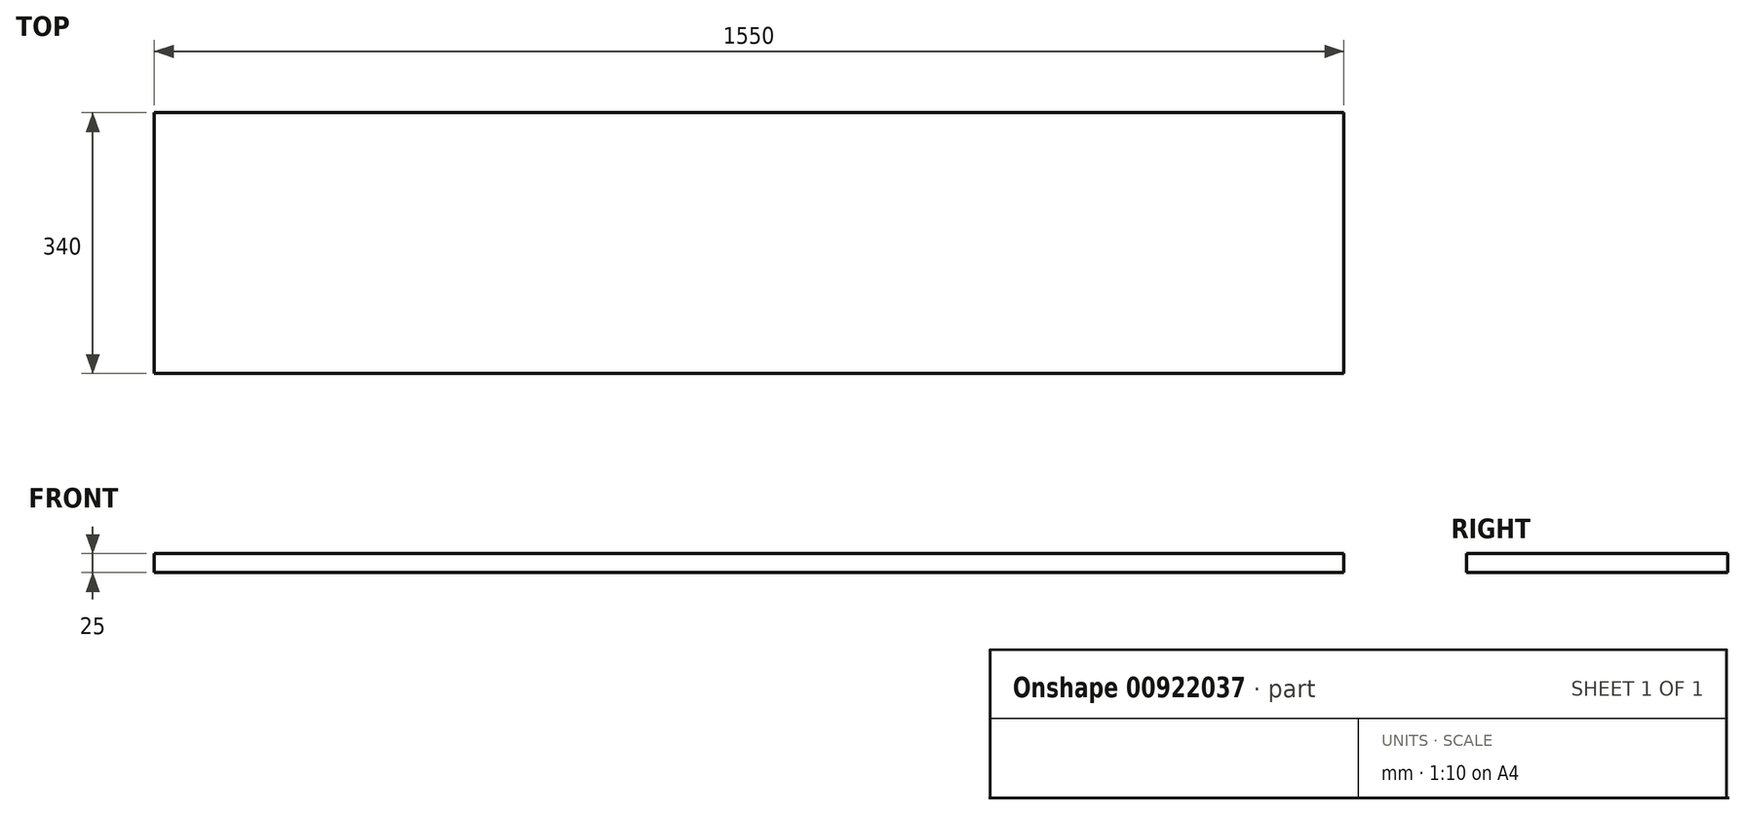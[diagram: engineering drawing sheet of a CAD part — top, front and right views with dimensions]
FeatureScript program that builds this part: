
annotation { "Feature Type Name" : "Feature", "Feature Type Description" : "" }
export const myFeature = defineFeature(function(context is Context, id is Id, definition is map)
    precondition{}
    {
        {
            var Q0;
            Q0=qCreatedBy(makeId("Top.planeOp"),FACE);
            var sketch = newSketch(context, id + "F0", { "sketchPlane" : qUnion([Q0])});
            skLineSegment(sketch, "E0.bottom", {"start": v(-775, 0) * mm, "end": v(775, 0) * mm});
            skLineSegment(sketch, "E0.top", {"start": v(-775, -340) * mm, "end": v(775, -340) * mm});
            skLineSegment(sketch, "E0.left", {"start": v(-775, 0) * mm, "end": v(-775, -340) * mm});
            skLineSegment(sketch, "E0.right", {"start": v(775, 0) * mm, "end": v(775, -340) * mm});
            skSolve(sketch);
        }
        {
            var Q0;
            Q0=makeQuery(id+"F0.imprint","IMPRINT",FACE,{"disambiguationData":[TD([[makeQuery(id+"F0.imprint","IMPRINT",EDGE,{"derivedFrom":sQuery(id+"F0.wireOp",EDGE,"E0.bottom")}),-1.0]])]});
            extrude(context, id + "F1", {"entities" : qUnion([Q0]), "depth" : 25 * mm, "offsetDistance" : 25 * mm});
        }
    });
